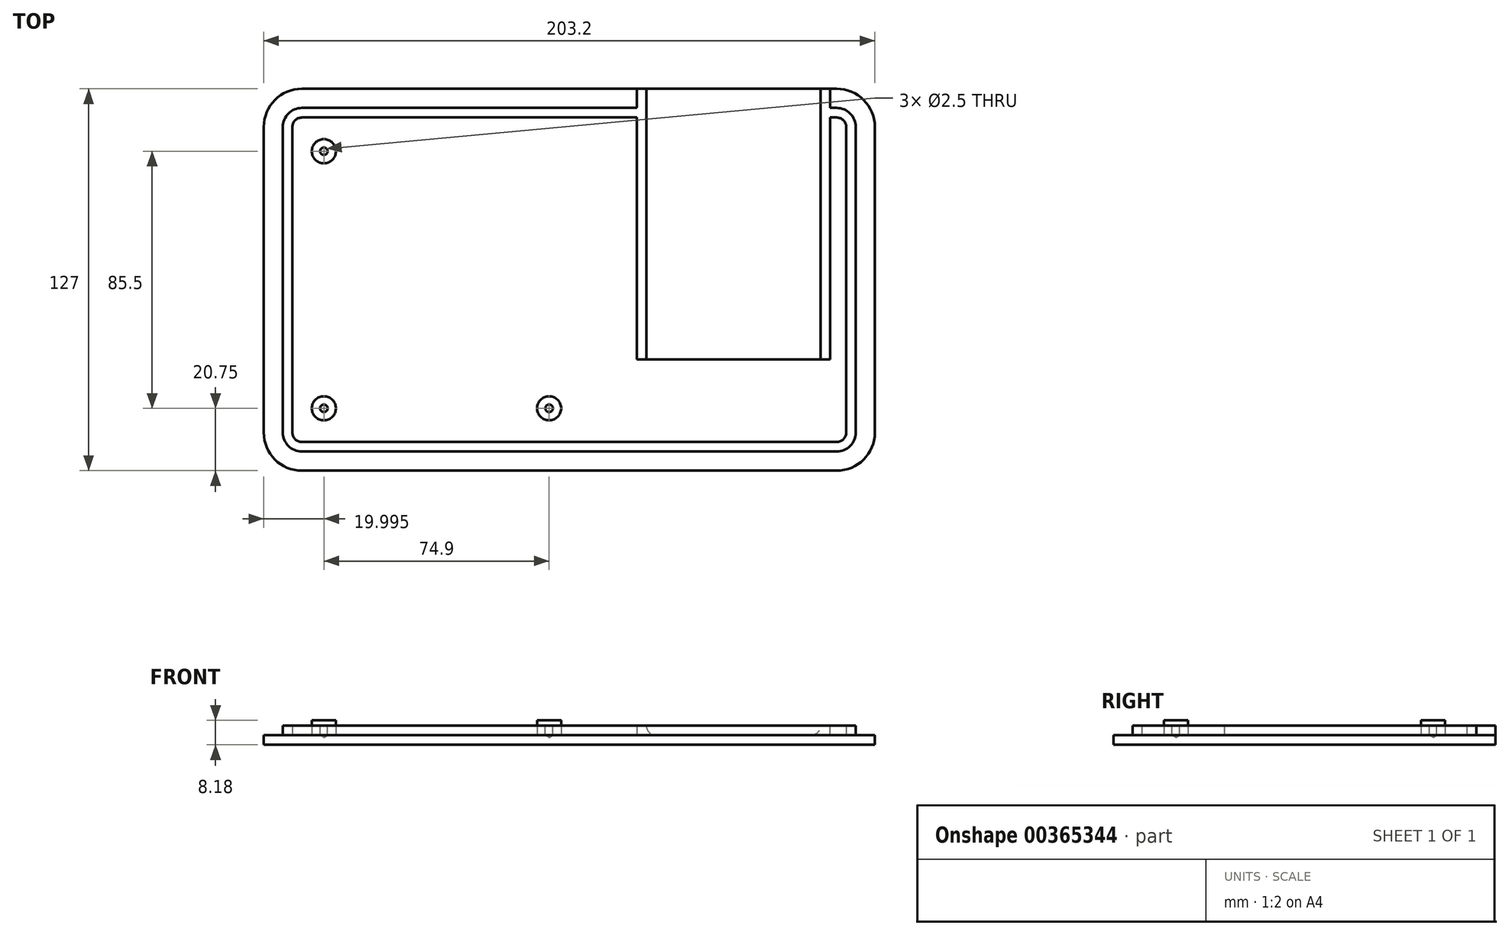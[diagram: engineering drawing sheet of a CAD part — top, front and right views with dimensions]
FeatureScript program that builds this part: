
annotation { "Feature Type Name" : "Feature", "Feature Type Description" : "" }
export const myFeature = defineFeature(function(context is Context, id is Id, definition is map)
    precondition{}
    {
        {
            var Q0;
            Q0=qCreatedBy(makeId("Top.planeOp"),FACE);
            var sketch = newSketch(context, id + "F0", { "sketchPlane" : qUnion([Q0])});
            skLineSegment(sketch, "E0.bottom", {"start": v(-101.6, 63.5) * mm, "end": v(101.6, 63.5) * mm});
            skLineSegment(sketch, "E0.top", {"start": v(-101.6, -63.5) * mm, "end": v(101.6, -63.5) * mm});
            skLineSegment(sketch, "E0.left", {"start": v(-101.6, 63.5) * mm, "end": v(-101.6, -63.5) * mm});
            skLineSegment(sketch, "E0.right", {"start": v(101.6, 63.5) * mm, "end": v(101.6, -63.5) * mm});
            skLineSegment(sketch, "E1", {"start": v(-101.6, -63.5) * mm, "end": v(101.6, 63.5) * mm, "construction": true});
            skSolve(sketch);
        }
        {
            var Q0;
            Q0=makeQuery(id+"F0.imprint","IMPRINT",FACE,{"disambiguationData":[TD([[makeQuery(id+"F0.imprint","IMPRINT",EDGE,{"derivedFrom":sQuery(id+"F0.wireOp",EDGE,"E0.bottom")}),-1.0]])]});
            extrude(context, id + "F1", {"entities" : qUnion([Q0]), "depth" : 3.17 * mm});
        }
        {
            var Q0;
            Q0=makeQuery(id+"F1.opExtrude","SWEPT_EDGE",EDGE,{"disambiguationData":[OSD([sQuery(id+"F0.wireOp",EDGE,"E0.top"),sQuery(id+"F0.wireOp",EDGE,"E0.left")])]});
            var Q1;
            Q1=makeQuery(id+"F1.opExtrude","SWEPT_EDGE",EDGE,{"disambiguationData":[OSD([sQuery(id+"F0.wireOp",EDGE,"E0.bottom"),sQuery(id+"F0.wireOp",EDGE,"E0.left")])]});
            var Q2;
            Q2=makeQuery(id+"F1.opExtrude","SWEPT_EDGE",EDGE,{"disambiguationData":[OSD([sQuery(id+"F0.wireOp",EDGE,"E0.top"),sQuery(id+"F0.wireOp",EDGE,"E0.right")])]});
            var Q3;
            Q3=makeQuery(id+"F1.opExtrude","SWEPT_EDGE",EDGE,{"disambiguationData":[OSD([sQuery(id+"F0.wireOp",EDGE,"E0.bottom"),sQuery(id+"F0.wireOp",EDGE,"E0.right")])]});
            fillet(context, id + "F2", {"entities" : qUnion([Q0, Q1, Q2, Q3]), "radius" : 12.7 * mm, "tangentPropagation" : true, "allowEdgeOverflow" : false});
        }
        {
            var Q0;
            Q0=makeQuery(id+"F1.opExtrude","CAP_FACE",FACE,{"disambiguationData":[OSD([sQuery(id+"F0.wireOp",EDGE,"E0.bottom"),sQuery(id+"F0.wireOp",EDGE,"E0.top"),sQuery(id+"F0.wireOp",EDGE,"E0.left"),sQuery(id+"F0.wireOp",EDGE,"E0.right")])],"isStart":false});
            var sketch = newSketch(context, id + "F3", { "sketchPlane" : qUnion([Q0])});
            skArc(sketch, "E2.0", {"start": v(-88.9, 57.15) * mm, "mid": v(-93.4, 55.3) * mm, "end": v(-95.25, 50.8) * mm});
            skLineSegment(sketch, "E2.1", {"start": v(-95.25, 50.8) * mm, "end": v(-95.25, -50.8) * mm});
            skLineSegment(sketch, "E2.2", {"start": v(-88.9, 57.15) * mm, "end": v(88.9, 57.15) * mm});
            skArc(sketch, "E2.3", {"start": v(-95.25, -50.8) * mm, "mid": v(-93.4, -55.3) * mm, "end": v(-88.9, -57.15) * mm});
            skArc(sketch, "E2.4", {"start": v(95.25, 50.8) * mm, "mid": v(93.4, 55.3) * mm, "end": v(88.9, 57.15) * mm});
            skLineSegment(sketch, "E2.5", {"start": v(95.25, 50.8) * mm, "end": v(95.25, -50.8) * mm});
            skArc(sketch, "E2.6", {"start": v(88.9, -57.15) * mm, "mid": v(93.4, -55.3) * mm, "end": v(95.25, -50.8) * mm});
            skLineSegment(sketch, "E2.7", {"start": v(-88.9, -57.15) * mm, "end": v(88.9, -57.15) * mm});
            skSolve(sketch);
        }
        {
            var Q0;
            Q0=makeQuery(id+"F3.imprint","IMPRINT",FACE,{"disambiguationData":[TD([[makeQuery(id+"F3.imprint","IMPRINT",EDGE,{"derivedFrom":sQuery(id+"F3.wireOp",EDGE,"E2.0")}),1.0]])]});
            extrude(context, id + "F4", {"entities" : qUnion([Q0]), "operationType" : NewBodyOperationType.ADD, "depth" : 3.17 * mm});
        }
        {
            var Q0;
            Q0=makeQuery(id+"F4.opExtrude","CAP_FACE",FACE,{"disambiguationData":[OSD([sQuery(id+"F3.wireOp",EDGE,"E2.0"),sQuery(id+"F3.wireOp",EDGE,"E2.1"),sQuery(id+"F3.wireOp",EDGE,"E2.2"),sQuery(id+"F3.wireOp",EDGE,"E2.3"),sQuery(id+"F3.wireOp",EDGE,"E2.4"),sQuery(id+"F3.wireOp",EDGE,"E2.5"),sQuery(id+"F3.wireOp",EDGE,"E2.6"),sQuery(id+"F3.wireOp",EDGE,"E2.7")])],"isStart":false});
            shell(context, id + "F5", {"entities" : qUnion([Q0]), "thickness" : 3.17 * mm});
        }
        {
            var Q0;
            Q0=makeQuery(id+"F5.opShell","OFFSET_FACE",FACE,{"disambiguationData":[OSD([sQuery(id+"F0.wireOp",EDGE,"E0.bottom"),sQuery(id+"F0.wireOp",EDGE,"E0.top"),sQuery(id+"F0.wireOp",EDGE,"E0.left"),sQuery(id+"F0.wireOp",EDGE,"E0.right")])]});
            var sketch = newSketch(context, id + "F6", { "sketchPlane" : qUnion([Q0])});
            skLineSegment(sketch, "E3.bottom", {"start": v(83.6, 53.98) * mm, "end": v(25.6, 53.98) * mm});
            skLineSegment(sketch, "E3.top", {"start": v(83.6, 63.5) * mm, "end": v(25.6, 63.5) * mm});
            skLineSegment(sketch, "E3.left", {"start": v(83.6, 53.98) * mm, "end": v(83.6, 63.5) * mm});
            skLineSegment(sketch, "E3.right", {"start": v(25.6, 53.98) * mm, "end": v(25.6, 63.5) * mm});
            skSolve(sketch);
        }
        {
            var Q0;
            Q0=makeQuery(id+"F6.imprint","IMPRINT",FACE,{"disambiguationData":[TD([[makeQuery(id+"F6.imprint","IMPRINT",EDGE,{"derivedFrom":sQuery(id+"F6.wireOp",EDGE,"vID5MLws-Pvfp-BZIT-HWvU-Rl9sqXq0lXm3.bottom")}),1.0]])]});
            var Q1;
            Q1=makeQuery(id+"F6.imprint","IMPRINT",FACE,{"disambiguationData":[TD([[makeQuery(id+"F6.imprint","IMPRINT",EDGE,{"derivedFrom":sQuery(id+"F6.wireOp",EDGE,"E3.bottom")}),-1.0]])]});
            extrude(context, id + "F7", {"entities" : qUnion([Q0, Q1]), "operationType" : NewBodyOperationType.REMOVE, "endBound" : BoundingType.THROUGH_ALL, "depth" : 25.4 * mm});
        }
        {
            var Q0;
            Q0=makeQuery(id+"F1.opExtrude","SWEPT_FACE",FACE,{"disambiguationData":[OSD([sQuery(id+"F0.wireOp",EDGE,"E0.bottom")])]});
            var sketch = newSketch(context, id + "F8", { "sketchPlane" : qUnion([Q0])});
            skLineSegment(sketch, "E4.bottom", {"start": v(-83.6, 0) * mm, "end": v(-25.6, 0) * mm});
            skLineSegment(sketch, "E4.left", {"start": v(-83.6, 0) * mm, "end": v(-83.6, 6.35) * mm});
            skLineSegment(sketch, "E4.right", {"start": v(-25.6, 0) * mm, "end": v(-25.6, 6.35) * mm});
            skArc(sketch, "E5", {"start": v(-83.6, 6.35) * mm, "mid": v(-82.72, 4.23) * mm, "end": v(-80.6, 3.35) * mm});
            skLineSegment(sketch, "E6", {"start": v(-80.6, 3.35) * mm, "end": v(-28.6, 3.35) * mm});
            skArc(sketch, "E7", {"start": v(-28.6, 3.35) * mm, "mid": v(-26.48, 4.23) * mm, "end": v(-25.6, 6.35) * mm});
            skSolve(sketch);
        }
        {
            var Q0;
            {var subQ0=sQuery(id+"F8.wireOp",EDGE,"E5");Q0=makeQuery(id+"F8.imprint","IMPRINT",FACE,{"disambiguationData":[TD([[makeQuery(id+"F8.imprint","IMPRINT",EDGE,{"derivedFrom":subQ0}),-1.0]])]});}
            var Q1;
            {var subQ0=sQuery(id+"F8.wireOp",EDGE,"E7");Q1=makeQuery(id+"F8.imprint","IMPRINT",FACE,{"disambiguationData":[TD([[makeQuery(id+"F8.imprint","IMPRINT",EDGE,{"derivedFrom":subQ0}),-1.0]])]});}
            extrude(context, id + "F9", {"entities" : qUnion([Q0, Q1]), "operationType" : NewBodyOperationType.ADD, "oppositeDirection" : true, "depth" : 90 * mm});
        }
        {
            var Q0;
            {var subQ0=sQuery(id+"F3.wireOp",EDGE,"E2.2");var subQ6=sQuery(id+"F8.wireOp",EDGE,"E4.right");Q0=makeQuery(id+"F9.boolean.opBoolean","SPLIT",FACE,{"disambiguationData":[TD([makeQuery(id+"F5.opShell","OFFSET_FACE",FACE,{"disambiguationData":[OSD([subQ0])]})])],"derivedFrom":makeQuery(id+"F9.opExtrude","SWEPT_FACE",FACE,{"disambiguationData":[OSD([subQ6])]})});}
            var Q1;
            {var subQ2=sQuery(id+"F8.wireOp",EDGE,"E4.right");var subQ3=sQuery(id+"F0.wireOp",EDGE,"E0.bottom");Q1=makeQuery(id+"F9.boolean.opBoolean","SPLIT",FACE,{"disambiguationData":[TD([makeQuery(id+"F1.opExtrude","SWEPT_FACE",FACE,{"disambiguationData":[OSD([subQ3])]})])],"derivedFrom":makeQuery(id+"F9.opExtrude","SWEPT_FACE",FACE,{"disambiguationData":[OSD([subQ2])]})});}
            extrude(context, id + "F10", {"entities" : qUnion([Q0, Q1]), "operationType" : NewBodyOperationType.ADD, "depth" : 3.17 * mm});
        }
        {
            var Q0;
            {var subQ0=sQuery(id+"F3.wireOp",EDGE,"E2.2");var subQ6=sQuery(id+"F8.wireOp",EDGE,"E4.left");Q0=makeQuery(id+"F9.boolean.opBoolean","SPLIT",FACE,{"disambiguationData":[TD([makeQuery(id+"F5.opShell","OFFSET_FACE",FACE,{"disambiguationData":[OSD([subQ0])]})])],"derivedFrom":makeQuery(id+"F9.opExtrude","SWEPT_FACE",FACE,{"disambiguationData":[OSD([subQ6])]})});}
            var Q1;
            {var subQ2=sQuery(id+"F8.wireOp",EDGE,"E4.left");var subQ3=sQuery(id+"F0.wireOp",EDGE,"E0.bottom");Q1=makeQuery(id+"F9.boolean.opBoolean","SPLIT",FACE,{"disambiguationData":[TD([makeQuery(id+"F1.opExtrude","SWEPT_FACE",FACE,{"disambiguationData":[OSD([subQ3])]})])],"derivedFrom":makeQuery(id+"F9.opExtrude","SWEPT_FACE",FACE,{"disambiguationData":[OSD([subQ2])]})});}
            extrude(context, id + "F11", {"entities" : qUnion([Q0, Q1]), "operationType" : NewBodyOperationType.ADD, "depth" : 3.17 * mm});
        }
        {
            var Q0;
            {var subQ3=sQuery(id+"F0.wireOp",EDGE,"E0.right");var subQ5=sQuery(id+"F0.wireOp",EDGE,"E0.left");var subQ6=sQuery(id+"F0.wireOp",EDGE,"E0.top");var subQ7=sQuery(id+"F0.wireOp",EDGE,"E0.bottom");Q0=makeQuery(id+"F9.boolean.opBoolean","SPLIT",FACE,{"disambiguationData":[TD([makeQuery(id+"F5.opShell","OFFSET_FACE",FACE,{"disambiguationData":[OSD([sQuery(id+"F3.wireOp",EDGE,"E2.0")])]})])],"derivedFrom":makeQuery(id+"F7.boolean.opBoolean","MERGE",FACE,{"derivedFrom":[makeQuery(id+"F1.opExtrude","CAP_FACE",FACE,{"disambiguationData":[OSD([subQ7,subQ6,subQ5,subQ3])],"isStart":false}),makeQuery(id+"F5.opShell","OFFSET_FACE",FACE,{"disambiguationData":[OSD([subQ7,subQ6,subQ5,subQ3])]}),makeQuery(id+"F7.opExtrude","CAP_FACE",FACE,{"disambiguationData":[OSD([sQuery(id+"F6.wireOp",EDGE,"vID5MLws-Pvfp-BZIT-HWvU-Rl9sqXq0lXm3.bottom"),sQuery(id+"F6.wireOp",EDGE,"vID5MLws-Pvfp-BZIT-HWvU-Rl9sqXq0lXm3.top"),sQuery(id+"F6.wireOp",EDGE,"vID5MLws-Pvfp-BZIT-HWvU-Rl9sqXq0lXm3.left"),sQuery(id+"F6.wireOp",EDGE,"vID5MLws-Pvfp-BZIT-HWvU-Rl9sqXq0lXm3.right")])],"isStart":true})]})});}
            var sketch = newSketch(context, id + "F12", { "sketchPlane" : qUnion([Q0])});
            skCircle(sketch, "E8", {"center": v(-81.6, 42.75) * mm, "radius": 4 * mm});
            skCircle(sketch, "E9", {"center": v(-81.6, -42.75) * mm, "radius": 4 * mm});
            skLineSegment(sketch, "E10", {"start": v(-81.6, 42.75) * mm, "end": v(-81.6, -42.75) * mm, "construction": true});
            skLineSegment(sketch, "E11", {"start": v(0, 0) * mm, "end": v(-81.6, 0) * mm, "construction": true});
            skLineSegment(sketch, "E12", {"start": v(-81.6, -42.75) * mm, "end": v(-6.7, -42.75) * mm, "construction": true});
            skCircle(sketch, "E13", {"center": v(-6.7, -42.75) * mm, "radius": 4 * mm});
            skSolve(sketch);
        }
        {
            var Q0;
            Q0=makeQuery(id+"F12.imprint","IMPRINT",FACE,{"disambiguationData":[TD([[makeQuery(id+"F12.imprint","IMPRINT",EDGE,{"derivedFrom":sQuery(id+"F12.wireOp",EDGE,"E9")}),1.0]])]});
            var Q1;
            Q1=makeQuery(id+"F12.imprint","IMPRINT",FACE,{"disambiguationData":[TD([[makeQuery(id+"F12.imprint","IMPRINT",EDGE,{"derivedFrom":sQuery(id+"F12.wireOp",EDGE,"E13")}),1.0]])]});
            var Q2;
            Q2=makeQuery(id+"F12.imprint","IMPRINT",FACE,{"disambiguationData":[TD([[makeQuery(id+"F12.imprint","IMPRINT",EDGE,{"derivedFrom":sQuery(id+"F12.wireOp",EDGE,"E8")}),1.0]])]});
            extrude(context, id + "F13", {"entities" : qUnion([Q0, Q1, Q2]), "operationType" : NewBodyOperationType.ADD, "depth" : 5 * mm});
        }
        {
            var Q0;
            Q0=makeQuery(id+"F13.opExtrude","CAP_FACE",FACE,{"disambiguationData":[OSD([sQuery(id+"F12.wireOp",EDGE,"E8")])],"isStart":false});
            var sketch = newSketch(context, id + "F14", { "sketchPlane" : qUnion([Q0])});
            skPoint(sketch, "E14", {"position": v(-81.6, 42.75) * mm});
            skSolve(sketch);
        }
        {
            var Q0;
            Q0=makeQuery(id+"F13.opExtrude","CAP_FACE",FACE,{"disambiguationData":[OSD([sQuery(id+"F12.wireOp",EDGE,"E9")])],"isStart":false});
            var sketch = newSketch(context, id + "F15", { "sketchPlane" : qUnion([Q0])});
            skPoint(sketch, "E15", {"position": v(-81.6, -42.75) * mm});
            skSolve(sketch);
        }
        {
            var Q0;
            Q0=makeQuery(id+"F13.opExtrude","CAP_FACE",FACE,{"disambiguationData":[OSD([sQuery(id+"F12.wireOp",EDGE,"E13")])],"isStart":false});
            var sketch = newSketch(context, id + "F16", { "sketchPlane" : qUnion([Q0])});
            skPoint(sketch, "E16", {"position": v(-6.7, -42.75) * mm});
            skSolve(sketch);
        }
        {
            var Q0;
            Q0=sQuery(id+"F14.wireOp",VERTEX,"E14");
            var Q1;
            Q1=sQuery(id+"F15.wireOp",VERTEX,"E15");
            var Q2;
            Q2=sQuery(id+"F16.wireOp",VERTEX,"E16");
            var Q3;
            Q3=makeQuery(id+"F1.opExtrude","SWEPT_BODY",BODY,{"disambiguationData":[OSD([sQuery(id+"F0.wireOp",EDGE,"E0.bottom"),sQuery(id+"F0.wireOp",EDGE,"E0.top"),sQuery(id+"F0.wireOp",EDGE,"E0.left"),sQuery(id+"F0.wireOp",EDGE,"E0.right")])]});
            hole(context, id + "F17", {"style" : HoleStyle.SIMPLE, "endStyle" : HoleEndStyle.BLIND, "standardTappedOrClearance" : lookupTablePath({ "standard" : "ISO", "engagement" : "75%", "pitch" : "0.5 mm", "size" : "M3", "type" : "Tapped" }), "standardBlindInLast" : lookupTablePath({ "standard" : "ISO", "engagement" : "75%", "pitch" : "0.5 mm", "size" : "M3", "type" : "Tapped" }), "holeDiameter" : 2.5 * mm, "showTappedDepth" : true, "holeDepth" : 5 * mm, "isTappedThrough" : true, "tappedDepth" : 3.5 * mm, "tapClearance" : 3, "locations" : qUnion([Q0, Q1, Q2]), "scope" : qUnion([Q3]), "majorDiameter" : 3 * mm});
        }
    });
